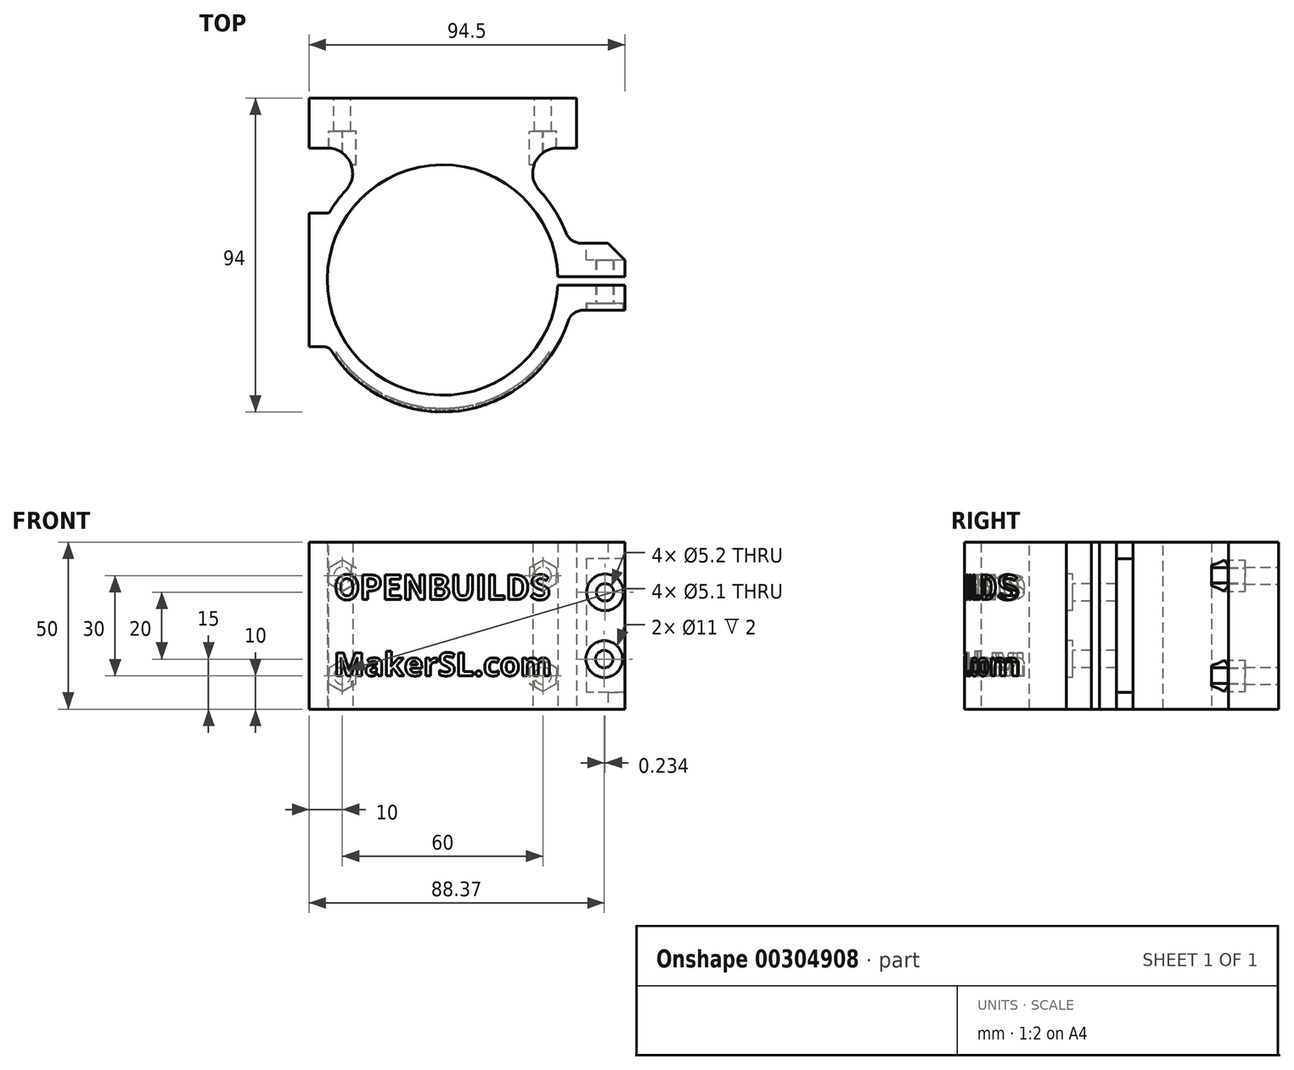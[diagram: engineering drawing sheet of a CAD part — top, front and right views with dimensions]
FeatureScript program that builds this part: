
annotation { "Feature Type Name" : "Feature", "Feature Type Description" : "" }
export const myFeature = defineFeature(function(context is Context, id is Id, definition is map)
    precondition{}
    {
        {
            var Q0;
            Q0=qCreatedBy(makeId("Top.planeOp"),FACE);
            var sketch = newSketch(context, id + "F0", { "sketchPlane" : qUnion([Q0])});
            skArc(sketch, "E0", {"start": v(34.49, 1) * mm, "mid": v(-34.5, 0.25) * mm, "end": v(34.47, -1.5) * mm});
            skArc(sketch, "E1", {"start": v(36.86, 14.2) * mm, "mid": v(33.5, 20.93) * mm, "end": v(28.93, 26.9) * mm});
            skLineSegment(sketch, "E2.bottom", {"start": v(40, 39.5) * mm, "end": v(34.42, 39.5) * mm});
            skLineSegment(sketch, "E2.top", {"start": v(40, 54.5) * mm, "end": v(-40, 54.5) * mm});
            skLineSegment(sketch, "E2.left", {"start": v(40, 39.5) * mm, "end": v(40, 54.5) * mm});
            skLineSegment(sketch, "E2.right", {"start": v(-40, 39.5) * mm, "end": v(-40, 54.5) * mm});
            skPoint(sketch, "E2.middle", {"position": v(0, 47) * mm});
            skLineSegment(sketch, "E3", {"start": v(0, 54.5) * mm, "end": v(0, 34.5) * mm});
            skLineSegment(sketch, "E4.bottom", {"start": v(54.5, -1.5) * mm, "end": v(34.47, -1.5) * mm});
            skLineSegment(sketch, "E4.top", {"start": v(54.5, 1) * mm, "end": v(34.49, 1) * mm});
            skPoint(sketch, "E4.middle", {"position": v(34.5, 0) * mm});
            skLineSegment(sketch, "E5.bottom", {"start": v(54.5, -9) * mm, "end": v(42.24, -9) * mm});
            skLineSegment(sketch, "E5.left", {"start": v(54.5, -9) * mm, "end": v(54.5, -1.5) * mm});
            skLineSegment(sketch, "E6.trimOffspring", {"start": v(54.5, 1) * mm, "end": v(54.5, 8.5) * mm});
            skPoint(sketch, "E7.visualSharp", {"position": v(38.78, 7.5) * mm});
            skPoint(sketch, "E8.visualSharp", {"position": v(38.46, -9) * mm});
            skArc(sketch, "E8.filletArc", {"start": v(42.24, -9) * mm, "mid": v(39.31, -9.95) * mm, "end": v(37.5, -12.43) * mm});
            skArc(sketch, "E9.trimOffspring", {"start": v(-28.93, 26.9) * mm, "mid": v(-20.12, -34) * mm, "end": v(37.5, -12.43) * mm});
            skLineSegment(sketch, "E10.trimOffspring", {"start": v(-34.42, 39.5) * mm, "end": v(-40, 39.5) * mm});
            skArc(sketch, "E11.filletArc", {"start": v(-28.93, 26.9) * mm, "mid": v(-27.55, 35) * mm, "end": v(-34.42, 39.5) * mm});
            skArc(sketch, "E12.filletArc", {"start": v(34.42, 39.5) * mm, "mid": v(27.55, 35) * mm, "end": v(28.93, 26.9) * mm});
            skLineSegment(sketch, "E13.top", {"start": v(54.5, 11) * mm, "end": v(41.52, 11) * mm});
            skLineSegment(sketch, "E13.left", {"start": v(54.5, 8.5) * mm, "end": v(54.5, 11) * mm});
            skPoint(sketch, "E14.visualSharp", {"position": v(37.94, 11) * mm});
            skArc(sketch, "E14.filletArc", {"start": v(36.86, 14.2) * mm, "mid": v(38.7, 11.88) * mm, "end": v(41.52, 11) * mm});
            skSolve(sketch);
        }
        {
            var Q0;
            {var subQ3=sQuery(id+"F0.wireOp",EDGE,"E2.right");Q0=makeQuery(id+"F0.imprint","IMPRINT",FACE,{"disambiguationData":[TD([[makeQuery(id+"F0.imprint","IMPRINT",EDGE,{"derivedFrom":subQ3}),-1.0]])]});}
            var Q1;
            Q1=makeQuery(id+"F0.imprint","IMPRINT",FACE,{"disambiguationData":[TD([[makeQuery(id+"F0.imprint","IMPRINT",EDGE,{"derivedFrom":sQuery(id+"F0.wireOp",EDGE,"E1")}),1.0]])]});
            extrude(context, id + "F1", {"entities" : qUnion([Q0, Q1]), "depth" : 50 * mm});
        }
        {
            var Q0;
            Q0=makeQuery(id+"F1.opExtrude","SWEPT_FACE",FACE,{"disambiguationData":[OSD([sQuery(id+"F0.wireOp",EDGE,"E2.top")])]});
            var sketch = newSketch(context, id + "F2", { "sketchPlane" : qUnion([Q0])});
            skLineSegment(sketch, "E15", {"start": v(-40, 10) * mm, "end": v(40, 10) * mm, "construction": true});
            skLineSegment(sketch, "E16", {"start": v(-40, 40) * mm, "end": v(40, 40) * mm, "construction": true});
            skCircle(sketch, "E17", {"center": v(-30, 10) * mm, "radius": 2.55 * mm});
            skCircle(sketch, "E18", {"center": v(-30, 40) * mm, "radius": 2.55 * mm});
            skCircle(sketch, "E19", {"center": v(30, 40) * mm, "radius": 2.55 * mm});
            skCircle(sketch, "E20", {"center": v(30, 10) * mm, "radius": 2.55 * mm});
            skSolve(sketch);
        }
        {
            var Q0;
            Q0=qSketchRegion(id+"F2",true);
            extrude(context, id + "F3", {"entities" : qUnion([Q0]), "operationType" : NewBodyOperationType.REMOVE, "oppositeDirection" : true, "depth" : 15 * mm});
        }
        {
            var Q0;
            Q0=qCreatedBy(makeId("Front.planeOp"),FACE);
            var sketch = newSketch(context, id + "F4", { "sketchPlane" : qUnion([Q0])});
            skLineSegment(sketch, "E21", {"start": v(0, 25) * mm, "end": v(57.85, 25) * mm});
            skArc(sketch, "E22.0.startCap", {"start": v(0, 22.5) * mm, "mid": v(-2.5, 25) * mm, "end": v(0, 27.5) * mm});
            skArc(sketch, "E22.0.endCap", {"start": v(57.85, 27.5) * mm, "mid": v(60.35, 25) * mm, "end": v(57.85, 22.5) * mm});
            skLineSegment(sketch, "E22.0.left", {"start": v(0, 27.5) * mm, "end": v(57.85, 27.5) * mm});
            skLineSegment(sketch, "E22.0.right", {"start": v(0, 22.5) * mm, "end": v(57.85, 22.5) * mm});
            skSolve(sketch);
        }
        {
            var Q0;
            {var subQ2=sQuery(id+"F0.wireOp",EDGE,"E5.bottom");Q0=makeQuery(id+"FSlxkKbNy0vXjha_1.boolean.opBoolean","SPLIT",FACE,{"disambiguationData":[TD([makeQuery(id+"FSlxkKbNy0vXjha_1.opExtrude","SWEPT_FACE",FACE,{"disambiguationData":[OSD([sQuery(id+"F4.wireOp",EDGE,"E22.0.left")])]})])],"derivedFrom":makeQuery(id+"F1.opExtrude","SWEPT_FACE",FACE,{"disambiguationData":[OSD([subQ2])]})});}
            var sketch = newSketch(context, id + "F5", { "sketchPlane" : qUnion([Q0])});
            skLineSegment(sketch, "E23", {"start": v(48.37, 50) * mm, "end": v(48.37, 0) * mm, "construction": true});
            skLineSegment(sketch, "E24", {"start": v(54.5, 15) * mm, "end": v(42.24, 15) * mm, "construction": true});
            skCircle(sketch, "E25", {"center": v(48.6, 35) * mm, "radius": 2.6 * mm});
            skCircle(sketch, "E26", {"center": v(48.37, 15) * mm, "radius": 2.6 * mm});
            skLineSegment(sketch, "E27", {"start": v(54.5, 25) * mm, "end": v(29.44, 25) * mm, "construction": true});
            skSolve(sketch);
        }
        {
            var Q0;
            Q0=makeQuery(id+"F5.imprint","IMPRINT",FACE,{"disambiguationData":[TD([[makeQuery(id+"F5.imprint","IMPRINT",EDGE,{"derivedFrom":sQuery(id+"F5.wireOp",EDGE,"E26")}),1.0]])]});
            var Q1;
            Q1=makeQuery(id+"F5.imprint","IMPRINT",FACE,{"disambiguationData":[TD([[makeQuery(id+"F5.imprint","IMPRINT",EDGE,{"derivedFrom":sQuery(id+"F5.wireOp",EDGE,"E25")}),1.0]])]});
            var Q2;
            Q2=makeQuery(id+"F5.imprint","IMPRINT",FACE,{"disambiguationData":[TD([[makeQuery(id+"F5.imprint","IMPRINT",EDGE,{"derivedFrom":sQuery(id+"F5.wireOp",EDGE,"r5i0Aljo-ERth-r3zv-b0hV-7ZURuQOSWyDo")}),1.0]])]});
            var Q3;
            Q3=makeQuery(id+"F5.imprint","IMPRINT",FACE,{"disambiguationData":[TD([[makeQuery(id+"F5.imprint","IMPRINT",EDGE,{"derivedFrom":sQuery(id+"F5.wireOp",EDGE,"pPAOFjSF-uRyi-eCdB-b1vO-61WpFvdSnZrL")}),1.0]])]});
            var Q4;
            {var subQ2=sQuery(id+"F0.wireOp",EDGE,"E4.bottom");Q4=makeQuery(id+"FSlxkKbNy0vXjha_1.boolean.opBoolean","SPLIT",FACE,{"disambiguationData":[TD([makeQuery(id+"FSlxkKbNy0vXjha_1.opExtrude","SWEPT_FACE",FACE,{"disambiguationData":[OSD([sQuery(id+"F4.wireOp",EDGE,"E22.0.right")])]})])],"derivedFrom":makeQuery(id+"F1.opExtrude","SWEPT_FACE",FACE,{"disambiguationData":[OSD([subQ2])]})});}
            extrude(context, id + "F6", {"entities" : qUnion([Q0, Q1, Q2, Q3]), "operationType" : NewBodyOperationType.REMOVE, "endBound" : BoundingType.THROUGH_ALL, "oppositeDirection" : true, "endBoundEntityFace" : qUnion([Q4]), "depth" : 25 * mm});
        }
        {
            var Q0;
            Q0=qCreatedBy(makeId("Right.planeOp"),FACE);
            var sketch = newSketch(context, id + "F7", { "sketchPlane" : qUnion([Q0])});
            skLineSegment(sketch, "E28", {"start": v(-2.5, 25) * mm, "end": v(-48.95, 25) * mm});
            skArc(sketch, "E29.0.startCap", {"start": v(-2.5, 27.5) * mm, "mid": v(0, 25) * mm, "end": v(-2.5, 22.5) * mm});
            skArc(sketch, "E29.0.endCap", {"start": v(-48.95, 22.5) * mm, "mid": v(-51.45, 25) * mm, "end": v(-48.95, 27.5) * mm});
            skLineSegment(sketch, "E29.0.left", {"start": v(-2.5, 22.5) * mm, "end": v(-48.95, 22.5) * mm});
            skLineSegment(sketch, "E29.0.right", {"start": v(-2.5, 27.5) * mm, "end": v(-48.95, 27.5) * mm});
            skSolve(sketch);
        }
        {
            var Q0;
            Q0=makeQuery(id+"F1.opExtrude","SWEPT_FACE",FACE,{"disambiguationData":[OSD([sQuery(id+"F0.wireOp",EDGE,"E2.top")])]});
            cPlane(context, id + "F8", {"entities" : qUnion([Q0]), "cplaneType" : CPlaneType.OFFSET, "offset" : 10 * mm, "oppositeDirection" : true, "width" : 150 * mm, "height" : 150 * mm});
        }
        {
            var Q0;
            Q0=qCreatedBy(id+"F8.planeOp",FACE);
            var sketch = newSketch(context, id + "F9", { "sketchPlane" : qUnion([Q0])});
            skCircle(sketch, "E30.cCircle", {"center": v(-30, 10) * mm, "radius": 4.05 * mm, "construction": true});
            skLineSegment(sketch, "E30.0", {"start": v(-26, 12.42) * mm, "end": v(-25.9, 7.75) * mm});
            skLineSegment(sketch, "E30.1", {"start": v(-25.9, 7.75) * mm, "end": v(-29.9, 5.32) * mm});
            skLineSegment(sketch, "E30.2", {"start": v(-29.9, 5.32) * mm, "end": v(-34, 7.58) * mm});
            skLineSegment(sketch, "E30.3", {"start": v(-34, 7.58) * mm, "end": v(-34.1, 12.25) * mm});
            skLineSegment(sketch, "E30.4", {"start": v(-34.1, 12.25) * mm, "end": v(-30.1, 14.68) * mm});
            skLineSegment(sketch, "E30.5", {"start": v(-30.1, 14.68) * mm, "end": v(-26, 12.42) * mm});
            skPoint(sketch, "E30.0.midPoint", {"position": v(-25.95, 10.09) * mm});
            skCircle(sketch, "E31.0.1.0", {"center": v(-30, 40) * mm, "radius": 4.05 * mm, "construction": true});
            skLineSegment(sketch, "E31.0.1.1", {"start": v(-25.9, 37.75) * mm, "end": v(-29.9, 35.32) * mm});
            skLineSegment(sketch, "E31.0.1.2", {"start": v(-30.1, 44.68) * mm, "end": v(-26, 42.42) * mm});
            skPoint(sketch, "E31.0.1.3", {"position": v(-25.95, 40.09) * mm});
            skLineSegment(sketch, "E31.0.1.4", {"start": v(-29.9, 35.32) * mm, "end": v(-34, 37.58) * mm});
            skLineSegment(sketch, "E31.0.1.5", {"start": v(-34.1, 42.25) * mm, "end": v(-30.1, 44.68) * mm});
            skLineSegment(sketch, "E31.0.1.6", {"start": v(-26, 42.42) * mm, "end": v(-25.9, 37.75) * mm});
            skLineSegment(sketch, "E31.0.1.7", {"start": v(-34, 37.58) * mm, "end": v(-34.1, 42.25) * mm});
            skCircle(sketch, "E31.1.0.0", {"center": v(30, 10) * mm, "radius": 4.05 * mm, "construction": true});
            skLineSegment(sketch, "E31.1.0.1", {"start": v(34.1, 7.75) * mm, "end": v(30.1, 5.32) * mm});
            skLineSegment(sketch, "E31.1.0.2", {"start": v(29.9, 14.68) * mm, "end": v(34, 12.42) * mm});
            skPoint(sketch, "E31.1.0.3", {"position": v(34.05, 10.09) * mm});
            skLineSegment(sketch, "E31.1.0.4", {"start": v(30.1, 5.32) * mm, "end": v(26, 7.58) * mm});
            skLineSegment(sketch, "E31.1.0.5", {"start": v(25.9, 12.25) * mm, "end": v(29.9, 14.68) * mm});
            skLineSegment(sketch, "E31.1.0.6", {"start": v(34, 12.42) * mm, "end": v(34.1, 7.75) * mm});
            skLineSegment(sketch, "E31.1.0.7", {"start": v(26, 7.58) * mm, "end": v(25.9, 12.25) * mm});
            skCircle(sketch, "E31.1.1.0", {"center": v(30, 40) * mm, "radius": 4.05 * mm, "construction": true});
            skLineSegment(sketch, "E31.1.1.1", {"start": v(34.1, 37.75) * mm, "end": v(30.1, 35.32) * mm});
            skLineSegment(sketch, "E31.1.1.2", {"start": v(29.9, 44.68) * mm, "end": v(34, 42.42) * mm});
            skPoint(sketch, "E31.1.1.3", {"position": v(34.05, 40.09) * mm});
            skLineSegment(sketch, "E31.1.1.4", {"start": v(30.1, 35.32) * mm, "end": v(26, 37.58) * mm});
            skLineSegment(sketch, "E31.1.1.5", {"start": v(25.9, 42.25) * mm, "end": v(29.9, 44.68) * mm});
            skLineSegment(sketch, "E31.1.1.6", {"start": v(34, 42.42) * mm, "end": v(34.1, 37.75) * mm});
            skLineSegment(sketch, "E31.1.1.7", {"start": v(26, 37.58) * mm, "end": v(25.9, 42.25) * mm});
            skLineSegment(sketch, "E31.direction1", {"start": v(-34, 7.58) * mm, "end": v(26, 7.58) * mm, "construction": true});
            skLineSegment(sketch, "E31.direction2", {"start": v(-34, 7.58) * mm, "end": v(-34, 37.58) * mm, "construction": true});
            skSolve(sketch);
        }
        {
            var Q0;
            Q0=qSketchRegion(id+"F9",true);
            extrude(context, id + "F10", {"entities" : qUnion([Q0]), "operationType" : NewBodyOperationType.REMOVE, "oppositeDirection" : true, "depth" : 10 * mm});
        }
        {
            var Q0;
            Q0=qCreatedBy(makeId("Front.planeOp"),FACE);
            cPlane(context, id + "F11", {"entities" : qUnion([Q0]), "cplaneType" : CPlaneType.OFFSET, "offset" : 50 * mm, "width" : 150 * mm, "height" : 150 * mm});
        }
        {
            var Q0;
            Q0=qCreatedBy(id+"F11.planeOp",FACE);
            var sketch = newSketch(context, id + "F12", { "sketchPlane" : qUnion([Q0])});
            skText(sketch, "E32", { "text": "OPENBUILDS", "fontName": "NotoSansCJKsc-Bold.otf"});
            skText(sketch, "E33", { "text": "MakerSL.com", "fontName": "OpenSans-Bold.ttf"});
            const initialGuessF12  = {"E32": [-0.0325, 0.0328, 1, 0, 0.0072], "E33": [-0.0325, 0.01, 1, 0, 0.00697]};
            skSetInitialGuess(sketch, initialGuessF12);
            skSolve(sketch);
        }
        {
            var Q0;
            Q0=qSketchRegion(id+"F12",true);
            extrude(context, id + "F13", {"entities" : qUnion([Q0]), "operationType" : NewBodyOperationType.REMOVE, "oppositeDirection" : true, "depth" : 50 * mm});
        }
        {
            var Q0;
            Q0=makeQuery(id+"F1.opExtrude","CAP_FACE",FACE,{"disambiguationData":[OSD([sQuery(id+"F0.wireOp",EDGE,"E0"),sQuery(id+"F0.wireOp",EDGE,"E1"),sQuery(id+"F0.wireOp",EDGE,"E2.bottom"),sQuery(id+"F0.wireOp",EDGE,"E2.top"),sQuery(id+"F0.wireOp",EDGE,"E2.left"),sQuery(id+"F0.wireOp",EDGE,"E2.right"),sQuery(id+"F0.wireOp",EDGE,"E4.bottom"),sQuery(id+"F0.wireOp",EDGE,"E4.top"),sQuery(id+"F0.wireOp",EDGE,"E5.bottom"),sQuery(id+"F0.wireOp",EDGE,"E5.left"),sQuery(id+"F0.wireOp",EDGE,"E6.trimOffspring"),sQuery(id+"F0.wireOp",EDGE,"E8.filletArc"),sQuery(id+"F0.wireOp",EDGE,"E9.trimOffspring"),sQuery(id+"F0.wireOp",EDGE,"E10.trimOffspring"),sQuery(id+"F0.wireOp",EDGE,"E11.filletArc"),sQuery(id+"F0.wireOp",EDGE,"E12.filletArc"),sQuery(id+"F0.wireOp",EDGE,"E13.top"),sQuery(id+"F0.wireOp",EDGE,"E13.left"),sQuery(id+"F0.wireOp",EDGE,"E14.filletArc")])],"isStart":false});
            var sketch = newSketch(context, id + "F14", { "sketchPlane" : qUnion([Q0])});
            skArc(sketch, "E34", {"start": v(-34.5, 0) * mm, "mid": v(-2.28, -34.42) * mm, "end": v(34.2, -4.54) * mm});
            skArc(sketch, "E35", {"start": v(-38.5, 0) * mm, "mid": v(-2.54, -38.42) * mm, "end": v(38.16, -5.07) * mm});
            skLineSegment(sketch, "E36", {"start": v(-34.5, 0) * mm, "end": v(-38.5, 0) * mm});
            skLineSegment(sketch, "E37", {"start": v(34.2, -4.54) * mm, "end": v(38.16, -5.07) * mm});
            skSolve(sketch);
        }
        {
            var Q0;
            Q0=makeQuery(id+"F14.imprint","IMPRINT",FACE,{"disambiguationData":[TD([[makeQuery(id+"F14.imprint","IMPRINT",EDGE,{"derivedFrom":sQuery(id+"F14.wireOp",EDGE,"E34")}),-1.0]])]});
            extrude(context, id + "F15", {"entities" : qUnion([Q0]), "operationType" : NewBodyOperationType.ADD, "oppositeDirection" : true, "depth" : 49 * mm});
        }
        {
            var Q0;
            Q0=makeQuery(id+"F1.opExtrude","SWEPT_FACE",FACE,{"disambiguationData":[OSD([sQuery(id+"F0.wireOp",EDGE,"E5.bottom")])]});
            var sketch = newSketch(context, id + "F16", { "sketchPlane" : qUnion([Q0])});
            skCircle(sketch, "E38", {"center": v(48.6, 35) * mm, "radius": 5.5 * mm});
            skCircle(sketch, "E39", {"center": v(48.37, 15) * mm, "radius": 5.5 * mm});
            skSolve(sketch);
        }
        {
            var Q0;
            Q0=makeQuery(id+"F16.imprint","IMPRINT",FACE,{"disambiguationData":[TD([[makeQuery(id+"F16.imprint","IMPRINT",EDGE,{"derivedFrom":sQuery(id+"F16.wireOp",EDGE,"E38")}),1.0]])]});
            var Q1;
            Q1=makeQuery(id+"F16.imprint","IMPRINT",FACE,{"disambiguationData":[TD([[makeQuery(id+"F16.imprint","IMPRINT",EDGE,{"derivedFrom":sQuery(id+"F16.wireOp",EDGE,"E39")}),1.0]])]});
            extrude(context, id + "F17", {"entities" : qUnion([Q0, Q1]), "operationType" : NewBodyOperationType.REMOVE, "oppositeDirection" : true, "depth" : 2 * mm});
        }
        {
            var Q0;
            Q0=makeQuery(id+"F1.opExtrude","SWEPT_FACE",FACE,{"disambiguationData":[OSD([sQuery(id+"F0.wireOp",EDGE,"E13.top")])]});
            var sketch = newSketch(context, id + "F18", { "sketchPlane" : qUnion([Q0])});
            skLineSegment(sketch, "E40", {"start": v(-48.6, 35) * mm, "end": v(-48.37, 15) * mm, "construction": true});
            skPoint(sketch, "E41.middle", {"position": v(-48.49, 25) * mm});
            skLineSegment(sketch, "E42.bottom", {"start": v(-58.09, 45) * mm, "end": v(-43, 45) * mm});
            skLineSegment(sketch, "E42.top", {"start": v(-58.09, 5) * mm, "end": v(-43, 5) * mm});
            skLineSegment(sketch, "E42.left", {"start": v(-58.09, 45) * mm, "end": v(-58.09, 5) * mm});
            skLineSegment(sketch, "E42.right", {"start": v(-43, 45) * mm, "end": v(-43, 5) * mm});
            skSolve(sketch);
        }
        {
            var Q0;
            Q0=makeQuery(id+"F18.imprint","IMPRINT",FACE,{"disambiguationData":[TD([[makeQuery(id+"F18.imprint","IMPRINT",EDGE,{"derivedFrom":sQuery(id+"F18.wireOp",EDGE,"E41.bottom")}),-1.0]])]});
            var Q1;
            {var subQ2=sQuery(id+"F18.wireOp",EDGE,"E42.right");Q1=makeQuery(id+"F18.imprint","IMPRINT",FACE,{"disambiguationData":[TD([[makeQuery(id+"F18.imprint","IMPRINT",EDGE,{"derivedFrom":subQ2}),-1.0]])]});}
            extrude(context, id + "F19", {"entities" : qUnion([Q0, Q1]), "operationType" : NewBodyOperationType.REMOVE, "oppositeDirection" : true, "depth" : 5 * mm});
        }
        {
            var Q0;
            {var subQ0=sQuery(id+"F0.wireOp",EDGE,"E13.left");var subQ1=sQuery(id+"F0.wireOp",EDGE,"E13.top");Q0=makeQuery(id+"F19.boolean.opBoolean","SPLIT",EDGE,{"disambiguationData":[TD([makeQuery(id+"F19.opExtrude","SWEPT_FACE",FACE,{"disambiguationData":[OSD([sQuery(id+"F18.wireOp",EDGE,"E42.bottom")])]})])],"derivedFrom":makeQuery(id+"F1.opExtrude","SWEPT_EDGE",EDGE,{"disambiguationData":[OSD([subQ1,subQ0])]})});}
            var Q1;
            {var subQ0=sQuery(id+"F0.wireOp",EDGE,"E13.left");var subQ1=sQuery(id+"F0.wireOp",EDGE,"E13.top");Q1=makeQuery(id+"F19.boolean.opBoolean","SPLIT",EDGE,{"disambiguationData":[TD([makeQuery(id+"F19.opExtrude","SWEPT_FACE",FACE,{"disambiguationData":[OSD([sQuery(id+"F18.wireOp",EDGE,"E42.top")])]})])],"derivedFrom":makeQuery(id+"F1.opExtrude","SWEPT_EDGE",EDGE,{"disambiguationData":[OSD([subQ1,subQ0])]})});}
            chamfer(context, id + "F20", {"entities" : qUnion([Q0, Q1]), "width" : 5 * mm, "tangentPropagation" : true});
        }
        {
            var Q0;
            Q0=makeQuery(id+"F1.opExtrude","CAP_FACE",FACE,{"disambiguationData":[OSD([sQuery(id+"F0.wireOp",EDGE,"E0"),sQuery(id+"F0.wireOp",EDGE,"E1"),sQuery(id+"F0.wireOp",EDGE,"E2.bottom"),sQuery(id+"F0.wireOp",EDGE,"E2.top"),sQuery(id+"F0.wireOp",EDGE,"E2.left"),sQuery(id+"F0.wireOp",EDGE,"E2.right"),sQuery(id+"F0.wireOp",EDGE,"E4.bottom"),sQuery(id+"F0.wireOp",EDGE,"E4.top"),sQuery(id+"F0.wireOp",EDGE,"E5.bottom"),sQuery(id+"F0.wireOp",EDGE,"E5.left"),sQuery(id+"F0.wireOp",EDGE,"E6.trimOffspring"),sQuery(id+"F0.wireOp",EDGE,"E8.filletArc"),sQuery(id+"F0.wireOp",EDGE,"E9.trimOffspring"),sQuery(id+"F0.wireOp",EDGE,"E10.trimOffspring"),sQuery(id+"F0.wireOp",EDGE,"E11.filletArc"),sQuery(id+"F0.wireOp",EDGE,"E12.filletArc"),sQuery(id+"F0.wireOp",EDGE,"E13.top"),sQuery(id+"F0.wireOp",EDGE,"E13.left"),sQuery(id+"F0.wireOp",EDGE,"E14.filletArc")])],"isStart":false});
            var sketch = newSketch(context, id + "F21", { "sketchPlane" : qUnion([Q0])});
            skLineSegment(sketch, "E43.bottom", {"start": v(-34.06, -20) * mm, "end": v(-40, -20) * mm});
            skLineSegment(sketch, "E43.top", {"start": v(-34.06, 20) * mm, "end": v(-40, 20) * mm});
            skPoint(sketch, "E43.middle", {"position": v(-39.5, 0) * mm});
            skPoint(sketch, "E44.orphan", {"position": v(-28.93, 26.9) * mm});
            skPoint(sketch, "E45.orphan", {"position": v(37.5, -12.43) * mm});
            skPoint(sketch, "E43.left.start.orphan", {"position": v(-24.5, -20) * mm});
            skPoint(sketch, "E46.orphan", {"position": v(-24.5, 20) * mm});
            skLineSegment(sketch, "E47", {"start": v(-40, 20) * mm, "end": v(-40, -20) * mm});
            skPoint(sketch, "E43.right.end.orphan", {"position": v(-54.5, 20) * mm});
            skPoint(sketch, "E48.orphan", {"position": v(-54.5, -20) * mm});
            skLineSegment(sketch, "E49", {"start": v(-34.06, 20) * mm, "end": v(-34.06, 10.18) * mm});
            skArc(sketch, "E50", {"start": v(-34.06, 10.18) * mm, "mid": v(-35.55, 0) * mm, "end": v(-34.06, -10.18) * mm});
            skLineSegment(sketch, "E51.trimOffspring", {"start": v(-34.06, -10.18) * mm, "end": v(-34.06, -20) * mm});
            skSolve(sketch);
        }
        {
            var Q0;
            {var subQ0=sQuery(id+"F21.wireOp",EDGE,"E43.bottom");Q0=makeQuery(id+"F21.imprint","IMPRINT",FACE,{"disambiguationData":[TD([[makeQuery(id+"F21.imprint","IMPRINT",EDGE,{"derivedFrom":subQ0}),-1.0]])]});}
            var Q1;
            {var subQ0=sQuery(id+"F21.wireOp",EDGE,"E49");Q1=makeQuery(id+"F21.imprint","IMPRINT",FACE,{"disambiguationData":[TD([[makeQuery(id+"F21.imprint","IMPRINT",EDGE,{"derivedFrom":subQ0}),-1.0]])]});}
            extrude(context, id + "F22", {"entities" : qUnion([Q0, Q1]), "operationType" : NewBodyOperationType.ADD, "oppositeDirection" : true, "depth" : 50 * mm});
        }
        {
            var Q0;
            Q0=makeQuery(id+"F22.opExtrude","SWEPT_EDGE",EDGE,{"disambiguationData":[OSD([sQuery(id+"F0.wireOp",EDGE,"E9.trimOffspring"),sQuery(id+"F21.wireOp",EDGE,"E43.top"),sQuery(id+"F21.wireOp",EDGE,"E49")])]});
            var Q1;
            Q1=makeQuery(id+"F22.opExtrude","SWEPT_EDGE",EDGE,{"disambiguationData":[OSD([sQuery(id+"F0.wireOp",EDGE,"E9.trimOffspring"),sQuery(id+"F21.wireOp",EDGE,"E43.bottom"),sQuery(id+"F21.wireOp",EDGE,"E51.trimOffspring")])]});
            fillet(context, id + "F23", {"entities" : qUnion([Q0, Q1]), "radius" : 2.5 * mm, "tangentPropagation" : true, "allowEdgeOverflow" : false});
        }
    });
